# Revit family: Haworth_UMA_Light
name_source: partatom
category: Lighting Fixtures
revit_build: Autodesk Revit 2018 (Build: 20170223_1515(x64)
units: mm (PartAtom-declared; Revit-internal decimal feet)

## family parameters
Always vertical = Yes
Cut with Voids When Loaded = No
Light Source = Yes
OmniClass Number = 23.80.70.11.14
OmniClass Title = General Luminaries, Directional
Part Type = Normal
Room Calculation Point = No
Round Connector Dimension = Use Diameter
Shared = No
Work Plane-Based = No

## types (1)
- HCPL-UMT2-11 - Audio Lantern
    Actual Depth = 6"
    Actual Height = 11"
    Actual Width = 6"
    Assembly Code = D5020200
    Base Finish = Haworth _ Paint _ Collection White
    Color Filter = 16777215
    Description = Haworth UMA Audio Lantern
    Dimming Lamp Color Temperature Shift = <None>
    Emit Shape Visible in Rendering = No
    Emit from Circle Diameter = 12"
    Glass Finish = Haworth _ UMA _ Glass
    Handle Finish = Haworth _ Leather _ Tan
    Manufacturer = Haworth
    Model = HCPL-UMT2
    Photometric Web File = generic
    Revision Number = 1
    Size = Verify Final Dim. w/ Haworth
    Speaker Finish = Haworth _ Metal _ Stainless Steel
    Tilt Angle = 90.00°
    URL = http://www.haworth.com
    URL - Product = https://www.haworth.com
    Warranty = http://www.haworth.com
    Wattage Comments = 4.5-12W 120V 60Hz

## geometry (parser evidence)
native form markers: Sweep x2
no freeform markers — native parametric forms only
